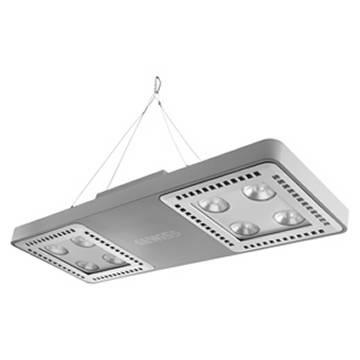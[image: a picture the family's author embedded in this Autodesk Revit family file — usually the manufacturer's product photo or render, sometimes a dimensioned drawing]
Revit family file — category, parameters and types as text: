
# Revit family: Lighting-Industriale-GEWISS-SMART[4]HLO_APPARECCHI-LED_2M
name_source: partatom
category: Apparecchi per illuminazione
units: mm (PartAtom-declared; Revit-internal decimal feet)

## family parameters
Basato su piano di lavoro = Sì
Condiviso = No
Numero OmniClass = 23.80.70.00
Punto di calcolo locali = No
Quota connettore circolare = Usa diametro
Sempre verticale = No
Sorgente d'illuminazione = No
Taglio con vuoti quando caricato = No
Tipo di parte = Normale
Titolo OmniClass = Lighting

## types (1)
- Lighting-Industriale-GEWISS-SMART[4]HLO_APPARECCHI-LED_2M
    Alimentatore = Incluso
    Apparecchio a ridotta temperatura superficiale = Si
    Applicazione = Interno
    Cablaggio = Con connettore stagno Gw connect
    Caratteristiche elettriche e gestione della luce = -
    Caratteristiche ottiche e illuminotecniche = -
    Carico apparente = 97 VA
    Catalogo = LIGHTING
    Certificazione DIN 18032-3 = Con Staffa - Kit Funi + morsetto (in approvazione)
    Certificazioni e classificazioni = -
    Classe fotobiologica = RG0
    Classe isolamento = I
    Classificazione = Lighting
    Classificazione: = -
    Codice Electrocod = 2444
    Codice digitale univoco (Datamatrix) = Datamatrix
    Colore = Grigio RAL 7035
    Commenti sul wattaggio = 97W
    Contesto = Illuminazione di industrie e impianti sportivi
    Controllo abbagliamento e luminanza = -
    Corpo = PA6 “Halogen Free” caricato fibra vetro
    Descrizione = SMART[4]HB 2M C.PAS.ON/OFF HLO ELL.57K
    Dispositivo di protezione = DM 6kV / CM 6kV
    Dist_sorg_lum = 10 mm  [stored 0.0328084 ft]
    Durata di vita = L90B10 (Tq+25°C) = 70.000 h - L90B10 (Tq+50°C) = 35.000 h
    Efficienza luminosa (lm/W) = 128
    Finitura colore = Grigio RAL 7035
    Fissaggio = -
    Frequenza nominale (Hz) = 50/60 Hz
    Gancio di chiusura = -
    Garanzia = 5 anni
    Grado di protezione = IP66
    Gruppo ottico = Riflettore in PC metallizzato e lenti in PMMA
    Guarnizioni = tipo siliconico antinvecchiamento
    IDF = 5274bbbe-5488-4b27-9c90-45de0a4a626a
    IDT = d6c0a54b56be4af78e01cdd4bdcb8af8
    IPEA = -
    Immagine tipo = GWL1311.jpg
    Inclinazione = Con accessorio staffa
    Indice di resa cromatica = CRI-80
    Informazioni generali = -
    Installazione e manutenzione = -
    Lampada = LED
    Larghezza = 254 mm
    Lumen output (lm) = 16000
    Lunghezza = 699 mm  [stored 2.29331 ft]
    Mascherina = <Per categoria>
    Materiali = -
    Modello = GWS4222BQ857
    Motore = <Per categoria>
    Norma di riferimento = EN 60598-1 ; EN 60598-2-1 ; EN 60598-2-24
    Ottica = Ellittica
    Peso (kg): = 6,5
    Potenza di sistema = 125W
    Produttore = GEWISS S.p.A.
    Prospetto di default = 1219 mm
    Resistenza agli urti = IK08
    Resistenza al filo incandescente = 850 °C
    SEO = High bay
    Scheda Tecnica = https://www.gewiss.com
    Schermo = Vetro Temprato Spessore 4mm
    Sistema di controllo = ON / OFF
    Sistema di controllo : = ON / OFF
    Sostituibilità gruppo ottico = Non sostituibile
    Sostituibilità piastra di cablaggio = Non sostituibile
    Spessore plafoniera = 40 mm  [stored 0.131234 ft]
    Struttura plafoniera = <Per categoria>
    Superficie massima esposta al vento : = 0,184 m²
    Temperatura di colore = 5700K
    Temperatura di esercizio = -30°C ÷ +50 °C
    Temperatura di stoccaggio = -40 +70 °C
    Tensione di alimentazione = 220 - 240 V
    Tipo di apparecchio = Riflettore industriale a LED&nbsp;
    Tipo di installazione e montaggio = Plafone - Parete - Sospensione
    Tipologia sorgente luminosa = LED - Non sostituibile
    Tolleranza cromatica = SDCM = 3
    Trasformatore = <Per categoria>
    URL = https://www.gewiss.com
    Vano di alimentazione = Integrato
    Versione file RFA = 20.11
    Viti esterne = Acciaio inox
    Voltaggio = 230 V

note: [stored X ft] marks values corroborated as IEEE doubles in the binary element streams (Revit-internal decimal feet)

## geometry (parser evidence)
native form markers: Blend x4, Sweep x3
no freeform markers — native parametric forms only
